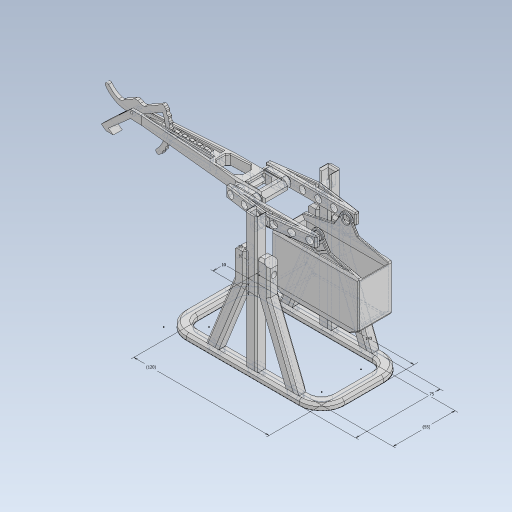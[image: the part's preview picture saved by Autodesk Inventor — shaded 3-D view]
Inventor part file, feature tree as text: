
AUTODESK INVENTOR PART (.ipt)
format: ipt  version: 2023 (Build 270158030, 158C)  size: 2,182,144 bytes
history: native  units: mm
features: extrude x40, chamfer x36, sketch x32, other x22, projected_geometry x18, fillet x12, mirror x11, plane x5, pattern_circular x2
ambient origin geometry x8: Origin, YZ Plane, XZ Plane, XY Plane, X Axis, Y Axis, Z Axis, Center Point
bodies: SOLID_WEIGHT (feature_tree)
feature tree (178):
  other  "baseplate"
  sketch  "Sketch1"  dims[d0=75.0mm d1=140.0mm]
  extrude  "Extrusion1"  Depth=140.0mm
  extrude  "Extrusion2"  Depth=10.0mm
  sketch  "Sketch3"  dims[d4=20.0mm d5=5.0mm d6=0.0mm]
  extrude  "Extrusion5"  Depth=5.0mm TaperAngle=0.0deg
  extrude  "Extrusion6"  Depth=2.0mm
  extrude  "Extrusion3"  Depth=3.0mm
  extrude  "Extrusion7"  Depth=10.0mm
  extrude  "Extrusion9"  TaperAngle=0.0deg  [1 undecoded]
  extrude  "Extrusion10"  Depth=120.0mm
  extrude  "Extrusion11"  Depth=0.01mm
  extrude  "Extrusion29"  Depth=10.0mm
  other  "center-mirror-plane"
  other  "Work Point1"
  plane  "Work Plane2"
  extrude  "Extrusion12"  Depth=25.0mm
  extrude  "Extrusion13"  Depth=5.0mm TaperAngle=0.0deg
  extrude  "Extrusion14"  Depth=10.0mm
  extrude  "Extrusion15"  Depth=10.0mm TaperAngle=0.0deg
  extrude  "Extrusion30"  Depth=5.0mm
  extrude  "Extrusion31"  Depth=6.5mm
  plane  "Work Plane5"
  extrude  "Extrusion32"  Depth=1.75mm
  extrude  "Extrusion33"  Depth=6.5mm
  extrude  "Extrusion34"  Depth=10.0mm
  fillet  "Fillet4"  Radius=3.2mm
  chamfer  "Chamfer37"  Distance=10.0mm
  extrude  "Extrusion35"  Depth=4.0mm
  chamfer  "Chamfer38"  [1 undecoded]
  fillet  "Fillet11"  Radius=21.0mm
  chamfer  "Chamfer39"  Distance=125.0mm
  fillet  "Fillet12"  Radius=10.0mm
  extrude  "Extrusion36"  Depth=4.0mm
  fillet  "Fillet5"  Radius=12.0mm
  extrude  "ratchet-extrusion"  TaperAngle=0.0deg  [1 undecoded]
  sketch  "Sketch51"  dims[d101=6.5mm]
  extrude  "Extrusion45"  Depth=4.0mm
  extrude  "Extrusion46"  Depth=4.0mm
  pattern_circular  "Circular Pattern3"  [2 undecoded]
  pattern_circular  "Circular Pattern4"  Angle=45.0deg  [1 undecoded]
  fillet  "Fillet13"  Radius=1.0mm
  fillet  "Fillet15"  Radius=1.5mm
  fillet  "Fillet10"  Radius=2.5mm
  extrude  "Extrusion17"  Depth=4.0mm
  extrude  "Extrusion26"  Depth=4.0mm
  extrude  "Extrusion38"  TaperAngle=0.0deg  [1 undecoded]
  extrude  "Extrusion47"  Depth=4.0mm
  fillet  "Fillet19"  Radius=2.0mm
  fillet  "Fillet16"  Radius=1.0mm
  chamfer  "Chamfer1"  Distance=1.5mm Angle=45.0deg
  chamfer  "Chamfer2"  Distance=1.5mm Angle=45.0deg
  chamfer  "Chamfer4"  Distance=2.0mm Angle=45.0deg
  chamfer  "Chamfer56"  Distance=1.5mm Angle=45.0deg
  extrude  "Extrusion19"  Depth=4.0mm
  chamfer  "Chamfer5"  Distance=8.0mm
  chamfer  "Chamfer8"  Distance=5.0mm
  chamfer  "Chamfer9"  Distance=28.0mm
  chamfer  "Chamfer10"  Distance=6.0mm
  extrude  "Extrusion39"  Depth=4.0mm
  mirror  "Mirror12"
  chamfer  "Chamfer11"  Distance=5.0mm
  chamfer  "Chamfer50"  Distance=28.0mm
  chamfer  "Chamfer12"  Distance=8.0mm
  plane  "Work Plane4"
  extrude  "CW-extrusion"  Depth=4.0mm
  mirror  "Mirror3"
  extrude  "Extrusion21"  Depth=4.0mm
  extrude  "Extrusion22"  Depth=4.0mm TaperAngle=0.0deg
  mirror  "Mirror4"
  chamfer  "Chamfer13"  Distance=2.0mm
  extrude  "Extrusion23"  Depth=1.5mm TaperAngle=0.0deg
  mirror  "Mirror5"
  chamfer  "Chamfer31"  Distance=1.5mm Angle=45.0deg
  chamfer  "Chamfer14"  Distance=1.5mm
  chamfer  "Chamfer17"  Distance=1.0mm Angle=45.0deg
  chamfer  "Chamfer18"  Distance=0.5mm Angle=45.0deg
  extrude  "Extrusion24"  Depth=0.5mm TaperAngle=45.0deg
  extrude  "Extrusion25"  TaperAngle=0.0deg  [1 undecoded]
  chamfer  "Chamfer20"  Distance=1.0mm
  chamfer  "Chamfer49"  Distance=1.0mm
  chamfer  "Chamfer21"  [1 undecoded]
  extrude  "Extrusion40"  Depth=4.0mm TaperAngle=45.0deg
  extrude  "Extrusion41"  Depth=4.0mm TaperAngle=45.0deg
  chamfer  "Chamfer22"  Distance=1.2mm Angle=45.0deg
  chamfer  "Chamfer44"  Distance=1.2mm
  chamfer  "Chamfer45"  Distance=3.0mm
  fillet  "Fillet3"  Radius=2.0mm
  mirror  "Mirror2"
  mirror  "Mirror1"
  plane  "Work Plane3"
  mirror  "Mirror6"
  mirror  "Mirror7"
  mirror  "Mirror8"
  chamfer  "Chamfer26"  Distance=2.0mm
  chamfer  "Chamfer27"  Distance=2.0mm
  extrude  "Extrusion43"  Depth=4.0mm
  mirror  "Mirror10"
  chamfer  "Chamfer47"  Distance=15.996982mm
  extrude  "Extrusion42"  Depth=4.0mm
  chamfer  "Chamfer48"  Distance=6.0mm
  mirror  "Mirror11"
  plane  "Work Plane6"
  chamfer  "Chamfer51"  Distance=6.0mm
  chamfer  "Chamfer52"  Distance=6.0mm
  fillet  "Fillet17"  Radius=5.0mm
  chamfer  "Chamfer53"  Distance=5.0mm
  chamfer  "Chamfer54"  Distance=14.0mm
  chamfer  "Chamfer55"  Distance=14.0mm
  fillet  "Fillet18"  [1 undecoded]
  chamfer  "Chamfer57"  Distance=3.5mm Angle=45.0deg
  chamfer  "Chamfer58"  Distance=3.5mm Angle=45.0deg
  sketch  "Sketch2"  dims[d2=10.0mm d3=10.0mm]
  sketch  "Sketch4"  dims[d7=6.0mm d9=2.0mm]
  projected_geometry  "Projected Loop1"
  other  "A-frame"
  sketch  "Sketch7"  dims[d10=10.0mm d11=3.0mm]
  projected_geometry  "Projected Loop2"
  other  "upright"
  sketch  "Sketch9"  dims[d12=1.75mm d13=6.0mm d14=10.0mm]
  projected_geometry  "Projected Loop3"
  sketch  "Sketch10"  dims[d15=60.0mm d16=0.0mm d17=0.0mm]
  sketch  "Sketch12"  dims[d18=55.0mm d19=120.0mm]
  sketch  "Sketch13"  dims[d22=0.1mm d23=0.01mm]
  sketch  "Sketch14"  dims[d24=5.0mm d25=0.0mm d38=10.0mm]
  other  "pivot"
  sketch  "Sketch16"  dims[d39=25.0mm d40=25.0mm]
  other  "throw-arm-top"
  sketch  "Sketch18"  dims[d41=0.1mm d42=5.0mm d43=5.0mm d44=0.0mm d45=0.0mm]
  sketch  "Sketch20"  dims[d47=10.0mm d50=10.0mm]
  sketch  "Sketch22"  dims[d51=120.0mm d52=0.0mm d53=10.0mm d54=0.0mm]
  other  "counterweight"
  projected_geometry  "Projected Loop5"
  sketch  "Sketch26"  dims[d60=5.0mm d61=5.0mm]
  projected_geometry  "Projected Loop6"
  sketch  "Sketch27"  dims[d64=0.0mm d65=0.0mm d66=6.5mm]
  projected_geometry  "Projected Loop7"
  sketch  "Sketch30"  dims[d67=1.75mm d68=1.75mm]
  other  "Pattern of pivot:1"
  other  "pivot-mirror"
  other  "Pattern of upright:2"
  other  "upright-mirror"
  other  "Pattern of A-frame:3"
  other  "A-frame-b"
  other  "Pattern of A-frame:4"
  other  "A-frame-c"
  other  "Pattern of A-frame-b:5"
  other  "A-frame-d"
  sketch  "Sketch31"  dims[d69=11.0mm d70=6.5mm]
  projected_geometry  "Projected Loop8"
  sketch  "Sketch32"  dims[d71=7.0mm d72=0.0mm d73=6.0mm d74=3.2mm d75=10.0mm d76=0.0mm]
  projected_geometry  "Projected Loop9"
  sketch  "Sketch34"  dims[d77=4.0mm d78=40.0mm]
  sketch  "Sketch36"  dims[d79=40.0mm]
  sketch  "Sketch37"  dims[d80=5.0mm]
  projected_geometry  "Projected Loop15"
  projected_geometry  "Projected Loop16"
  sketch  "Sketch39"  dims[d83=4.0mm]
  sketch  "Sketch40"  dims[d84=29.0mm]
  projected_geometry  "Projected Loop17"
  sketch  "Sketch43"  dims[d85=2.0mm d86=8.0mm d87=0.0mm d88=0.0mm]
  other  "ratchet"
  sketch  "Sketch44"  dims[d89=6.0mm]
  sketch  "Sketch45"  dims[d90=5.0mm]
  projected_geometry  "Projected Loop18"
  sketch  "Sketch46"  dims[d91=5.0mm d92=0.0mm d93=0.0mm d96=21.0mm]
  projected_geometry  "Projected Loop20"
  sketch  "Sketch48"  dims[d99=8.0mm]
  other  "spacer-a"
  other  "Pattern of spacer-a:6"
  other  "spacer-b"
  projected_geometry  "Projected Loop24"
  sketch  "Sketch49"  dims[d100=10.0mm]
  projected_geometry  "Projected Loop25"
  projected_geometry  "Projected Loop26"
  projected_geometry  "Projected Loop27"
  sketch  "Sketch52"  dims[d102=6.5mm d103=125.0mm d104=10.0mm d105=5.0mm d106=0.0mm d107=0.0mm d108=7.0mm d109=12.0mm d110=0.0mm d111=0.0mm d119=6.0mm d120=5.0mm d121=10.0mm d122=0.0mm d126=1.0mm d127=2.0mm d128=45.0deg d129=1.0mm d130=2.0mm d131=45.0deg d135=1.5mm d136=2.0mm d137=45.0deg d138=2.5mm d139=2.8mm d140=12.0mm d141=0.0mm d142=0.0mm d144=6.0mm d145=2.0mm d146=2.0mm d147=45.0deg d155=1.0mm d156=2.0mm d157=45.0deg d158=1.5mm d159=2.0mm d160=45.0deg d162=1.5mm d163=2.0mm d164=45.0deg d165=2.0mm d166=2.0mm d167=45.0deg d168=1.5mm d169=2.0mm d170=45.0deg d172=2.0mm d173=8.0mm d174=5.0mm d175=28.0mm d176=6.0mm d177=40.0mm d178=5.0mm d179=28.0mm d180=8.0mm d181=8.0mm d182=2.0mm d183=2.0mm d184=0.0mm d185=2.0mm d186=0.0mm d187=1.5mm d188=0.0mm d189=1.5mm d190=2.0mm d191=45.0deg d195=1.0mm d196=1.5mm d197=0.0mm d200=1.0mm d201=2.0mm d202=45.0deg d209=0.5mm d210=2.0mm d211=45.0deg d212=0.5mm d213=2.0mm d214=45.0deg d221=0.0mm d222=0.0mm d223=1.0mm d224=1.0mm d227=0.0mm d228=0.0mm d232=4.0mm d233=2.0mm d234=45.0deg d235=1.0mm d236=2.0mm d237=45.0deg d238=1.2mm d239=2.0mm d240=45.0deg d241=1.2mm d242=3.0mm d247=2.0mm d248=2.0mm d249=2.0mm d250=0.9mm d254=15.996982mm d255=8.0mm d256=6.0mm d257=6.0mm d258=6.0mm d259=5.0mm d260=5.0mm d261=14.0mm d262=14.0mm d263=0.0mm d264=0.0mm d271=3.5mm d272=2.0mm d273=45.0deg d274=3.5mm d275=2.0mm d276=45.0deg d287=1.5mm d288=2.0mm d289=45.0deg d290=1.9mm d291=10.0mm d292=0.0mm d298=3.0mm d299=0.5mm d300=0.0mm d303=3.5mm d304=3.0mm d305=0.5mm d306=0.0mm d307=2.1mm d310=0.0mm d311=0.0mm d312=5.2mm d313=10.0mm d314=0.8mm d315=27.1mm d316=3.2mm d317=0.0mm d319=0.0mm d320=0.0mm d321=36.0mm d322=0.4mm d323=0.4mm d324=3.5mm d328=3.2mm d329=0.0mm d331=4.0mm d337=3.2mm d338=0.0mm d343=3.2mm d344=3.2mm d345=3.2mm d346=3.2mm d347=3.2mm d348=3.2mm d349=3.2mm d350=3.2mm d351=1.9mm d352=0.0mm d353=4.0mm d363=19.6mm d364=19.5mm d366=3.0mm d367=90.0deg d368=23.0mm d377=10.0mm d386=2.9mm d387=0.0mm d394=1.7mm d396=4.4mm d398=3.5mm d399=2.0mm d400=45.0deg d401=3.0mm d402=2.0mm d403=45.0deg d404=4.0mm d405=2.5mm d406=2.0mm d407=45.0deg d408=4.0mm d415=4.0mm d426=1.5mm d431=7.0mm d432=0.0mm d433=0.0mm d434=4.0mm d438=1.0mm d439=2.4mm d440=0.0mm d441=0.8mm d447=14.0mm d448=14.0mm d449=14.0mm d450=10.0mm d451=0.0mm d454=4.0mm d455=0.0mm d456=2.0mm d457=2.0mm d458=45.0deg d459=0.7mm d460=2.0mm d461=45.0deg d465=12.0mm d466=12.0mm d467=5.0mm d468=25.0mm d469=5.0mm d470=3.0mm d471=0.8mm d472=2.0mm d473=45.0deg d474=1.5mm d475=0.15mm d476=5.0mm d477=0.0mm d478=0.6mm d479=2.0mm d480=45.0deg d481=5.0mm d483=38.5mm d484=38.5mm d485=2.5mm d491=2.0mm d492=30.0deg d493=14.0mm d494=0.5mm d495=2.0mm d496=45.0deg d497=2.5mm d498=2.5mm d499=30.0deg d500=1.5mm d501=0.0mm d505=11.0mm d506=5.0mm d507=2.0mm d508=45.0deg d510=75.0deg d512=0.4mm d514=10.293981mm d520=1.5mm d521=63.0mm d522=3.2mm d524=4.0mm d525=75.0deg d526=35.0mm d527=5.072433mm d528=2.3mm d529=4.5mm d530=1.2mm d531=2.9mm d532=0.0mm d533=1.5mm d534=0.0mm d535=0.0mm d542=40.0mm d543=4.363323mm d545=50.0mm d546=5.759587mm d548=5.5mm d549=38.0mm d550=10.902886mm d551=5.0mm d552=2.0mm d553=45.0deg d554=1.0mm d555=2.0mm d556=45.0deg d557=2.0mm d558=2.0mm d559=0.0mm d560=1.0mm d561=2.0mm d562=45.0deg d563=1.9mm d564=2.0mm d565=45.0deg d566=1.6mm d567=2.0mm d568=45.0deg d570=7.0mm d572=7.504916mm d574=27.229453mm d575=2.0mm d576=0.95mm d577=0.7mm d578=4.362765mm d579=28.01763mm d580=40.653421mm d581=6.0mm d582=3.2mm d583=30.0deg d584=3.0mm d591=0.9mm d592=0.9mm d593=39.249188mm d594=1.5mm d595=1.5mm d596=3.0mm d597=3.0mm d598=5.0mm d599=2.501152mm d600=2.562412mm d601=3.0mm d602=90.0mm d603=10.765796mm d604=0.5mm d605=2.0mm d606=45.0deg d607=1.5mm d608=1.5mm d609=1.0mm d610=2.0mm d611=45.0deg d612=4.5mm d613=0.0mm d614=0.0mm d615=1.5mm d616=4.0mm d617=2.0mm d618=45.0deg]
  projected_geometry  "Projected Loop28"
note: 10 required parameter values undecoded (feature->parameter linkage not recoverable at this tier; creation-order binding heuristic only, values carry confidence <= 0.55)
